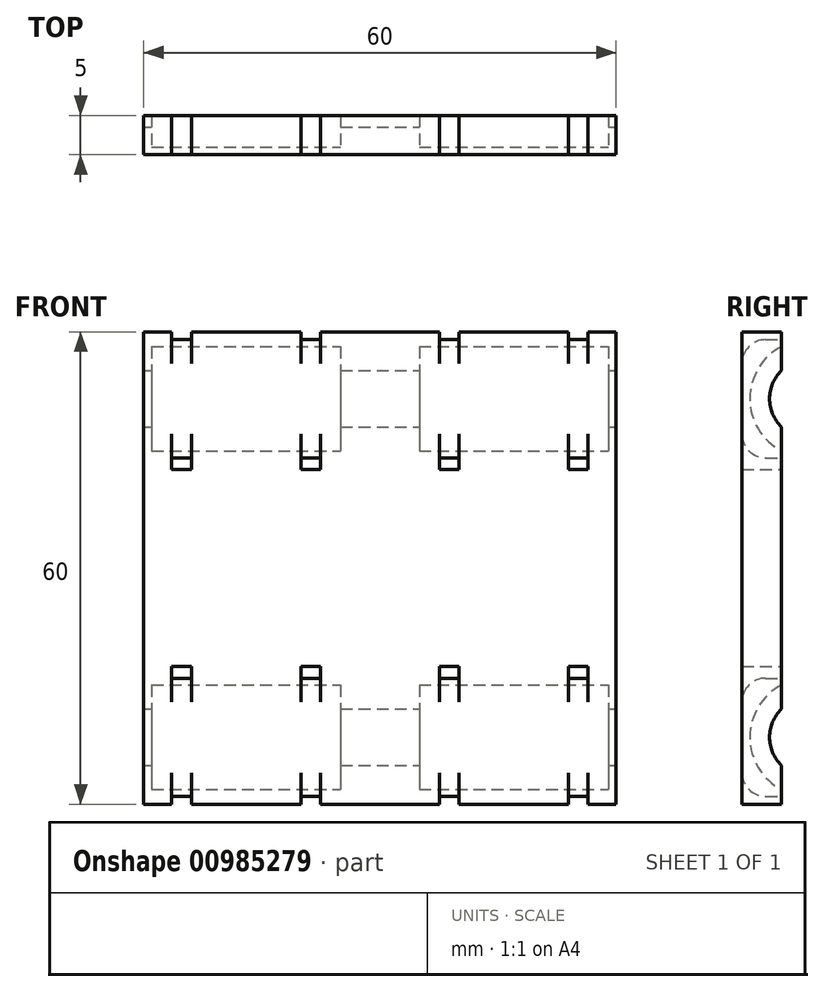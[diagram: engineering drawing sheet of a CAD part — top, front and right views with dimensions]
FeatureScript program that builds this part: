
annotation { "Feature Type Name" : "Feature", "Feature Type Description" : "" }
export const myFeature = defineFeature(function(context is Context, id is Id, definition is map)
    precondition{}
    {
        {
            var Q0;
            Q0=qCreatedBy(makeId("Front.planeOp"),FACE);
            var sketch = newSketch(context, id + "F0", { "sketchPlane" : qUnion([Q0])});
            skLineSegment(sketch, "E0.bottom", {"start": v(30, 30) * mm, "end": v(-30, 30) * mm});
            skLineSegment(sketch, "E0.top", {"start": v(30, -30) * mm, "end": v(-30, -30) * mm});
            skLineSegment(sketch, "E0.left", {"start": v(30, 30) * mm, "end": v(30, -30) * mm});
            skLineSegment(sketch, "E0.right", {"start": v(-30, 30) * mm, "end": v(-30, -30) * mm});
            skPoint(sketch, "E0.middle", {"position": v(0, 0) * mm});
            skSolve(sketch);
        }
        {
            var Q0;
            Q0 = qSketchRegion(id + "F0", true);
            extrude(context, id + "F1", {"entities" : qUnion([Q0]), "depth" : 5 * mm, "offsetDistance" : 25 * mm});
        }
        {
            var Q0;
            Q0=makeQuery(id+"F1.opExtrude","SWEPT_FACE",FACE,{"disambiguationData":[OSD([sQuery(id+"F0.wireOp",EDGE,"E0.left")])]});
            var sketch = newSketch(context, id + "F2", { "sketchPlane" : qUnion([Q0])});
            skCircle(sketch, "E1", {"center": v(3.5, 21.5) * mm, "radius": 7.5 * mm});
            skCircle(sketch, "E2.MirrorC", {"center": v(3.5, -21.5) * mm, "radius": 7.5 * mm});
            skSolve(sketch);
        }
        {
            var Q0;
            Q0 = qSketchRegion(id + "F2", true);
            extrude(context, id + "F3", {"entities" : qUnion([Q0]), "operationType" : NewBodyOperationType.REMOVE, "endBound" : BoundingType.THROUGH_ALL, "oppositeDirection" : true, "depth" : 25 * mm, "offsetDistance" : 25 * mm});
        }
        {
            var Q0;
            {var subQ0=sQuery(id+"F0.wireOp",EDGE,"E0.left");var subQ1=sQuery(id+"F0.wireOp",EDGE,"E0.right");Q0=makeQuery(id+"F3.boolean.opBoolean","SPLIT",FACE,{"disambiguationData":[TD([makeQuery(id+"F1.opExtrude","SWEPT_FACE",FACE,{"disambiguationData":[OSD([subQ0])]}),makeQuery(id+"F1.opExtrude","SWEPT_FACE",FACE,{"disambiguationData":[OSD([subQ1])]}),makeQuery(id+"F3.opExtrude","SWEPT_FACE",FACE,{"disambiguationData":[OSD([sQuery(id+"F2.wireOp",EDGE,"E1")])]}),makeQuery(id+"F3.opExtrude","SWEPT_FACE",FACE,{"disambiguationData":[OSD([sQuery(id+"F2.wireOp",EDGE,"E2.MirrorC")])]})])],"derivedFrom":makeQuery(id+"F1.opExtrude","CAP_FACE",FACE,{"disambiguationData":[OSD([sQuery(id+"F0.wireOp",EDGE,"E0.bottom"),sQuery(id+"F0.wireOp",EDGE,"E0.top"),subQ0,subQ1])],"isStart":true})});}
            var sketch = newSketch(context, id + "F4", { "sketchPlane" : qUnion([Q0])});
            skLineSegment(sketch, "E3.bottom", {"start": v(-30, 30) * mm, "end": v(-29, 30) * mm});
            skLineSegment(sketch, "E3.top", {"start": v(-30, -30) * mm, "end": v(-29, -30) * mm});
            skLineSegment(sketch, "E3.left", {"start": v(-30, 30) * mm, "end": v(-30, -30) * mm});
            skLineSegment(sketch, "E3.right", {"start": v(-29, 30) * mm, "end": v(-29, -30) * mm});
            skLineSegment(sketch, "E4.bottom", {"start": v(-5, 30) * mm, "end": v(5, 30) * mm});
            skLineSegment(sketch, "E4.top", {"start": v(-5, -30) * mm, "end": v(5, -30) * mm});
            skLineSegment(sketch, "E4.left", {"start": v(-5, 30) * mm, "end": v(-5, -30) * mm});
            skLineSegment(sketch, "E4.right", {"start": v(5, 30) * mm, "end": v(5, -30) * mm});
            skLineSegment(sketch, "E5.bottom", {"start": v(29, 30) * mm, "end": v(30, 30) * mm});
            skLineSegment(sketch, "E5.top", {"start": v(29, -30) * mm, "end": v(30, -30) * mm});
            skLineSegment(sketch, "E5.left", {"start": v(29, 30) * mm, "end": v(29, -30) * mm});
            skLineSegment(sketch, "E5.right", {"start": v(30, 30) * mm, "end": v(30, -30) * mm});
            skSolve(sketch);
        }
        {
            var Q0;
            Q0 = qSketchRegion(id + "F4", true);
            extrude(context, id + "F5", {"entities" : qUnion([Q0]), "operationType" : NewBodyOperationType.ADD, "oppositeDirection" : true, "depth" : 5 * mm, "offsetDistance" : 25 * mm});
        }
        {
            var Q0;
            Q0=makeQuery(id+"F5.boolean.opBoolean","MERGE",FACE,{"derivedFrom":[makeQuery(id+"F1.opExtrude","SWEPT_FACE",FACE,{"disambiguationData":[OSD([sQuery(id+"F0.wireOp",EDGE,"E0.left")])]}),makeQuery(id+"F5.opExtrude","SWEPT_FACE",FACE,{"disambiguationData":[OSD([sQuery(id+"F4.wireOp",EDGE,"E3.left")])]})]});
            var sketch = newSketch(context, id + "F6", { "sketchPlane" : qUnion([Q0])});
            skCircle(sketch, "E6", {"center": v(3.5, 21.5) * mm, "radius": 5 * mm});
            skCircle(sketch, "E7.MirrorC", {"center": v(3.5, -21.5) * mm, "radius": 5 * mm});
            skSolve(sketch);
        }
        {
            var Q0;
            Q0 = qSketchRegion(id + "F6", true);
            extrude(context, id + "F7", {"entities" : qUnion([Q0]), "operationType" : NewBodyOperationType.REMOVE, "endBound" : BoundingType.THROUGH_ALL, "oppositeDirection" : true, "depth" : 25 * mm, "offsetDistance" : 25 * mm});
        }
        {
            var Q0;
            {var subQ0=sQuery(id+"F4.wireOp",EDGE,"E3.left");var subQ1=sQuery(id+"F4.wireOp",EDGE,"E5.left");var subQ2=sQuery(id+"F4.wireOp",EDGE,"E3.right");var subQ3=sQuery(id+"F0.wireOp",EDGE,"E0.left");var subQ4=makeQuery(id+"F1.opExtrude","SWEPT_FACE",FACE,{"disambiguationData":[OSD([subQ3])]});var subQ5=sQuery(id+"F4.wireOp",EDGE,"E5.right");var subQ6=sQuery(id+"F0.wireOp",EDGE,"E0.right");var subQ7=makeQuery(id+"F1.opExtrude","SWEPT_FACE",FACE,{"disambiguationData":[OSD([subQ6])]});var subQ8=sQuery(id+"F4.wireOp",EDGE,"E4.left");var subQ9=makeQuery(id+"F3.opExtrude","SWEPT_FACE",FACE,{"disambiguationData":[OSD([sQuery(id+"F2.wireOp",EDGE,"E1")])]});var subQ10=sQuery(id+"F4.wireOp",EDGE,"E4.right");var subQ11=makeQuery(id+"F3.opExtrude","SWEPT_FACE",FACE,{"disambiguationData":[OSD([sQuery(id+"F2.wireOp",EDGE,"E2.MirrorC")])]});var subQ12=sQuery(id+"F0.wireOp",EDGE,"E0.top");var subQ13=sQuery(id+"F0.wireOp",EDGE,"E0.bottom");var subQ14=makeQuery(id+"F1.opExtrude","CAP_FACE",FACE,{"disambiguationData":[OSD([subQ13,subQ12,subQ3,subQ6])],"isStart":true});Q0=makeQuery(id+"F7.boolean.opBoolean","SPLIT",FACE,{"disambiguationData":[TD([subQ4,subQ7,makeQuery(id+"F3.boolean.opBoolean","COPY",FACE,{"derivedFrom":subQ9}),makeQuery(id+"F3.boolean.opBoolean","COPY",FACE,{"derivedFrom":subQ11}),makeQuery(id+"F5.opExtrude","SWEPT_FACE",FACE,{"disambiguationData":[OSD([subQ0])]}),makeQuery(id+"F5.opExtrude","SWEPT_FACE",FACE,{"disambiguationData":[OSD([subQ2])]}),makeQuery(id+"F5.opExtrude","SWEPT_FACE",FACE,{"disambiguationData":[OSD([subQ8])]}),makeQuery(id+"F5.opExtrude","SWEPT_FACE",FACE,{"disambiguationData":[OSD([subQ10])]}),makeQuery(id+"F5.opExtrude","SWEPT_FACE",FACE,{"disambiguationData":[OSD([subQ1])]}),makeQuery(id+"F5.opExtrude","SWEPT_FACE",FACE,{"disambiguationData":[OSD([subQ5])]}),makeQuery(id+"F7.opExtrude","SWEPT_FACE",FACE,{"disambiguationData":[OSD([sQuery(id+"F6.wireOp",EDGE,"E6")])]}),makeQuery(id+"F7.opExtrude","SWEPT_FACE",FACE,{"disambiguationData":[OSD([sQuery(id+"F6.wireOp",EDGE,"E7.MirrorC")])]})])],"derivedFrom":makeQuery(id+"F5.boolean.opBoolean","MERGE",FACE,{"derivedFrom":[makeQuery(id+"F3.boolean.opBoolean","SPLIT",FACE,{"disambiguationData":[TD([makeQuery(id+"F1.opExtrude","SWEPT_FACE",FACE,{"disambiguationData":[OSD([subQ13])]}),subQ4,subQ7,subQ9])],"derivedFrom":subQ14}),makeQuery(id+"F3.boolean.opBoolean","SPLIT",FACE,{"disambiguationData":[TD([makeQuery(id+"F1.opExtrude","SWEPT_FACE",FACE,{"disambiguationData":[OSD([subQ12])]}),subQ4,subQ7,subQ11])],"derivedFrom":subQ14}),makeQuery(id+"F3.boolean.opBoolean","SPLIT",FACE,{"disambiguationData":[TD([subQ4,subQ7,subQ9,subQ11])],"derivedFrom":subQ14}),makeQuery(id+"F5.opExtrude","CAP_FACE",FACE,{"disambiguationData":[OSD([sQuery(id+"F4.wireOp",EDGE,"E3.bottom"),sQuery(id+"F4.wireOp",EDGE,"E3.top"),subQ0,subQ2])],"isStart":true}),makeQuery(id+"F5.opExtrude","CAP_FACE",FACE,{"disambiguationData":[OSD([sQuery(id+"F4.wireOp",EDGE,"E4.bottom"),sQuery(id+"F4.wireOp",EDGE,"E4.top"),subQ8,subQ10])],"isStart":true}),makeQuery(id+"F5.opExtrude","CAP_FACE",FACE,{"disambiguationData":[OSD([sQuery(id+"F4.wireOp",EDGE,"E5.bottom"),sQuery(id+"F4.wireOp",EDGE,"E5.top"),subQ1,subQ5])],"isStart":true})]})});}
            var sketch = newSketch(context, id + "F8", { "sketchPlane" : qUnion([Q0])});
            skLineSegment(sketch, "E8.bottom", {"start": v(-26.45, 14) * mm, "end": v(-23.95, 14) * mm});
            skLineSegment(sketch, "E8.top", {"start": v(-26.45, 12.5) * mm, "end": v(-23.95, 12.5) * mm});
            skLineSegment(sketch, "E8.left", {"start": v(-26.45, 14) * mm, "end": v(-26.45, 12.5) * mm});
            skLineSegment(sketch, "E8.right", {"start": v(-23.95, 14) * mm, "end": v(-23.95, 12.5) * mm});
            skLineSegment(sketch, "E9.bottom", {"start": v(-10.05, 14) * mm, "end": v(-7.55, 14) * mm});
            skLineSegment(sketch, "E9.top", {"start": v(-10.05, 12.5) * mm, "end": v(-7.55, 12.5) * mm});
            skLineSegment(sketch, "E9.left", {"start": v(-10.05, 14) * mm, "end": v(-10.05, 12.5) * mm});
            skLineSegment(sketch, "E9.right", {"start": v(-7.55, 14) * mm, "end": v(-7.55, 12.5) * mm});
            skLineSegment(sketch, "E10.bottom", {"start": v(-10.05, 30.5) * mm, "end": v(-7.55, 30.5) * mm});
            skLineSegment(sketch, "E10.top", {"start": v(-10.05, 29) * mm, "end": v(-7.55, 29) * mm});
            skLineSegment(sketch, "E10.left", {"start": v(-10.05, 30.5) * mm, "end": v(-10.05, 29) * mm});
            skLineSegment(sketch, "E10.right", {"start": v(-7.55, 30.5) * mm, "end": v(-7.55, 29) * mm});
            skLineSegment(sketch, "E11.bottom", {"start": v(-26.45, 30.5) * mm, "end": v(-23.95, 30.5) * mm});
            skLineSegment(sketch, "E11.top", {"start": v(-26.45, 29) * mm, "end": v(-23.95, 29) * mm});
            skLineSegment(sketch, "E11.left", {"start": v(-26.45, 30.5) * mm, "end": v(-26.45, 29) * mm});
            skLineSegment(sketch, "E11.right", {"start": v(-23.95, 30.5) * mm, "end": v(-23.95, 29) * mm});
            skLineSegment(sketch, "E12", {"start": v(-34.92, 21.5) * mm, "end": v(-1.44, 21.5) * mm, "construction": true});
            skLineSegment(sketch, "E13.MirrorCS", {"start": v(26.45, 30.5) * mm, "end": v(26.45, 29) * mm});
            skLineSegment(sketch, "E14.MirrorCS", {"start": v(10.05, 14) * mm, "end": v(10.05, 12.5) * mm});
            skLineSegment(sketch, "E15.MirrorCS", {"start": v(7.55, 14) * mm, "end": v(7.55, 12.5) * mm});
            skLineSegment(sketch, "E16.MirrorCS", {"start": v(10.05, 30.5) * mm, "end": v(10.05, 29) * mm});
            skLineSegment(sketch, "E17.MirrorCS", {"start": v(23.95, 30.5) * mm, "end": v(23.95, 29) * mm});
            skLineSegment(sketch, "E18.MirrorCS", {"start": v(7.55, 30.5) * mm, "end": v(7.55, 29) * mm});
            skLineSegment(sketch, "E19.MirrorCS", {"start": v(23.95, 14) * mm, "end": v(23.95, 12.5) * mm});
            skLineSegment(sketch, "E20.MirrorCS", {"start": v(26.45, 14) * mm, "end": v(26.45, 12.5) * mm});
            skLineSegment(sketch, "E21.MirrorCS", {"start": v(10.05, 12.5) * mm, "end": v(7.55, 12.5) * mm});
            skLineSegment(sketch, "E22.MirrorCS", {"start": v(10.05, 14) * mm, "end": v(7.55, 14) * mm});
            skLineSegment(sketch, "E23.MirrorCS", {"start": v(26.45, 30.5) * mm, "end": v(23.95, 30.5) * mm});
            skLineSegment(sketch, "E24.MirrorCS", {"start": v(10.05, 29) * mm, "end": v(7.55, 29) * mm});
            skLineSegment(sketch, "E25.MirrorCS", {"start": v(26.45, 12.5) * mm, "end": v(23.95, 12.5) * mm});
            skLineSegment(sketch, "E26.MirrorCS", {"start": v(10.05, 30.5) * mm, "end": v(7.55, 30.5) * mm});
            skLineSegment(sketch, "E27.MirrorCS", {"start": v(26.45, 14) * mm, "end": v(23.95, 14) * mm});
            skLineSegment(sketch, "E28.MirrorCS", {"start": v(26.45, 29) * mm, "end": v(23.95, 29) * mm});
            skLineSegment(sketch, "E29.MirrorCS", {"start": v(-7.55, -14) * mm, "end": v(-7.55, -12.5) * mm});
            skLineSegment(sketch, "E30.MirrorCS", {"start": v(7.55, -30.5) * mm, "end": v(7.55, -29) * mm});
            skLineSegment(sketch, "E31.MirrorCS", {"start": v(23.95, -14) * mm, "end": v(23.95, -12.5) * mm});
            skLineSegment(sketch, "E32.MirrorCS", {"start": v(23.95, -30.5) * mm, "end": v(23.95, -29) * mm});
            skLineSegment(sketch, "E33.MirrorCS", {"start": v(10.05, -14) * mm, "end": v(10.05, -12.5) * mm});
            skLineSegment(sketch, "E34.MirrorCS", {"start": v(-26.45, -14) * mm, "end": v(-26.45, -12.5) * mm});
            skLineSegment(sketch, "E35.MirrorCS", {"start": v(-23.95, -30.5) * mm, "end": v(-23.95, -29) * mm});
            skLineSegment(sketch, "E36.MirrorCS", {"start": v(-7.55, -30.5) * mm, "end": v(-7.55, -29) * mm});
            skLineSegment(sketch, "E37.MirrorCS", {"start": v(-10.05, -30.5) * mm, "end": v(-10.05, -29) * mm});
            skLineSegment(sketch, "E38.MirrorCS", {"start": v(7.55, -14) * mm, "end": v(7.55, -12.5) * mm});
            skLineSegment(sketch, "E39.MirrorCS", {"start": v(-10.05, -14) * mm, "end": v(-10.05, -12.5) * mm});
            skLineSegment(sketch, "E40.MirrorCS", {"start": v(26.45, -30.5) * mm, "end": v(26.45, -29) * mm});
            skLineSegment(sketch, "E41.MirrorCS", {"start": v(-23.95, -14) * mm, "end": v(-23.95, -12.5) * mm});
            skLineSegment(sketch, "E42.MirrorCS", {"start": v(10.05, -30.5) * mm, "end": v(10.05, -29) * mm});
            skLineSegment(sketch, "E43.MirrorCS", {"start": v(26.45, -14) * mm, "end": v(26.45, -12.5) * mm});
            skLineSegment(sketch, "E44.MirrorCS", {"start": v(-26.45, -30.5) * mm, "end": v(-26.45, -29) * mm});
            skLineSegment(sketch, "E45.MirrorCS", {"start": v(-26.45, -12.5) * mm, "end": v(-23.95, -12.5) * mm});
            skLineSegment(sketch, "E46.MirrorCS", {"start": v(-10.05, -30.5) * mm, "end": v(-7.55, -30.5) * mm});
            skLineSegment(sketch, "E47.MirrorCS", {"start": v(-26.45, -14) * mm, "end": v(-23.95, -14) * mm});
            skLineSegment(sketch, "E48.MirrorCS", {"start": v(-10.05, -29) * mm, "end": v(-7.55, -29) * mm});
            skLineSegment(sketch, "E49.MirrorCS", {"start": v(-10.05, -14) * mm, "end": v(-7.55, -14) * mm});
            skLineSegment(sketch, "E50.MirrorCS", {"start": v(-26.45, -30.5) * mm, "end": v(-23.95, -30.5) * mm});
            skLineSegment(sketch, "E51.MirrorCS", {"start": v(10.05, -30.5) * mm, "end": v(7.55, -30.5) * mm});
            skLineSegment(sketch, "E52.MirrorCS", {"start": v(26.45, -29) * mm, "end": v(23.95, -29) * mm});
            skLineSegment(sketch, "E53.MirrorCS", {"start": v(10.05, -14) * mm, "end": v(7.55, -14) * mm});
            skLineSegment(sketch, "E54.MirrorCS", {"start": v(10.05, -12.5) * mm, "end": v(7.55, -12.5) * mm});
            skLineSegment(sketch, "E55.MirrorCS", {"start": v(-10.05, -12.5) * mm, "end": v(-7.55, -12.5) * mm});
            skLineSegment(sketch, "E56.MirrorCS", {"start": v(26.45, -14) * mm, "end": v(23.95, -14) * mm});
            skLineSegment(sketch, "E57.MirrorCS", {"start": v(26.45, -12.5) * mm, "end": v(23.95, -12.5) * mm});
            skLineSegment(sketch, "E58.MirrorCS", {"start": v(-26.45, -29) * mm, "end": v(-23.95, -29) * mm});
            skLineSegment(sketch, "E59.MirrorCS", {"start": v(26.45, -30.5) * mm, "end": v(23.95, -30.5) * mm});
            skLineSegment(sketch, "E60.MirrorCS", {"start": v(10.05, -29) * mm, "end": v(7.55, -29) * mm});
            skSolve(sketch);
        }
        {
            var Q0;
            Q0 = qSketchRegion(id + "F8", true);
            extrude(context, id + "F9", {"entities" : qUnion([Q0]), "operationType" : NewBodyOperationType.REMOVE, "endBound" : BoundingType.THROUGH_ALL, "oppositeDirection" : true, "depth" : 25 * mm, "offsetDistance" : 25 * mm});
        }
        {
            var Q0;
            Q0=makeQuery(id+"F9.boolean.opBoolean","INTERSECT",EDGE,{"derivedFrom":[makeQuery(id+"F1.opExtrude","CAP_FACE",FACE,{"disambiguationData":[OSD([sQuery(id+"F0.wireOp",EDGE,"E0.bottom"),sQuery(id+"F0.wireOp",EDGE,"E0.top"),sQuery(id+"F0.wireOp",EDGE,"E0.left"),sQuery(id+"F0.wireOp",EDGE,"E0.right")])],"isStart":false}),makeQuery(id+"F9.opExtrude","SWEPT_FACE",FACE,{"disambiguationData":[OSD([sQuery(id+"F8.wireOp",EDGE,"E58.MirrorCS")])]})]});
            var Q1;
            Q1=makeQuery(id+"F9.boolean.opBoolean","INTERSECT",EDGE,{"derivedFrom":[makeQuery(id+"F1.opExtrude","CAP_FACE",FACE,{"disambiguationData":[OSD([sQuery(id+"F0.wireOp",EDGE,"E0.bottom"),sQuery(id+"F0.wireOp",EDGE,"E0.top"),sQuery(id+"F0.wireOp",EDGE,"E0.left"),sQuery(id+"F0.wireOp",EDGE,"E0.right")])],"isStart":false}),makeQuery(id+"F9.opExtrude","SWEPT_FACE",FACE,{"disambiguationData":[OSD([sQuery(id+"F8.wireOp",EDGE,"E47.MirrorCS")])]})]});
            var Q2;
            Q2=makeQuery(id+"F9.boolean.opBoolean","INTERSECT",EDGE,{"derivedFrom":[makeQuery(id+"F1.opExtrude","CAP_FACE",FACE,{"disambiguationData":[OSD([sQuery(id+"F0.wireOp",EDGE,"E0.bottom"),sQuery(id+"F0.wireOp",EDGE,"E0.top"),sQuery(id+"F0.wireOp",EDGE,"E0.left"),sQuery(id+"F0.wireOp",EDGE,"E0.right")])],"isStart":false}),makeQuery(id+"F9.opExtrude","SWEPT_FACE",FACE,{"disambiguationData":[OSD([sQuery(id+"F8.wireOp",EDGE,"E49.MirrorCS")])]})]});
            var Q3;
            Q3=makeQuery(id+"F9.boolean.opBoolean","INTERSECT",EDGE,{"derivedFrom":[makeQuery(id+"F1.opExtrude","CAP_FACE",FACE,{"disambiguationData":[OSD([sQuery(id+"F0.wireOp",EDGE,"E0.bottom"),sQuery(id+"F0.wireOp",EDGE,"E0.top"),sQuery(id+"F0.wireOp",EDGE,"E0.left"),sQuery(id+"F0.wireOp",EDGE,"E0.right")])],"isStart":false}),makeQuery(id+"F9.opExtrude","SWEPT_FACE",FACE,{"disambiguationData":[OSD([sQuery(id+"F8.wireOp",EDGE,"E48.MirrorCS")])]})]});
            var Q4;
            Q4=makeQuery(id+"F9.boolean.opBoolean","INTERSECT",EDGE,{"derivedFrom":[makeQuery(id+"F1.opExtrude","CAP_FACE",FACE,{"disambiguationData":[OSD([sQuery(id+"F0.wireOp",EDGE,"E0.bottom"),sQuery(id+"F0.wireOp",EDGE,"E0.top"),sQuery(id+"F0.wireOp",EDGE,"E0.left"),sQuery(id+"F0.wireOp",EDGE,"E0.right")])],"isStart":false}),makeQuery(id+"F9.opExtrude","SWEPT_FACE",FACE,{"disambiguationData":[OSD([sQuery(id+"F8.wireOp",EDGE,"E60.MirrorCS")])]})]});
            var Q5;
            Q5=makeQuery(id+"F9.boolean.opBoolean","INTERSECT",EDGE,{"derivedFrom":[makeQuery(id+"F1.opExtrude","CAP_FACE",FACE,{"disambiguationData":[OSD([sQuery(id+"F0.wireOp",EDGE,"E0.bottom"),sQuery(id+"F0.wireOp",EDGE,"E0.top"),sQuery(id+"F0.wireOp",EDGE,"E0.left"),sQuery(id+"F0.wireOp",EDGE,"E0.right")])],"isStart":false}),makeQuery(id+"F9.opExtrude","SWEPT_FACE",FACE,{"disambiguationData":[OSD([sQuery(id+"F8.wireOp",EDGE,"E53.MirrorCS")])]})]});
            var Q6;
            Q6=makeQuery(id+"F9.boolean.opBoolean","INTERSECT",EDGE,{"derivedFrom":[makeQuery(id+"F1.opExtrude","CAP_FACE",FACE,{"disambiguationData":[OSD([sQuery(id+"F0.wireOp",EDGE,"E0.bottom"),sQuery(id+"F0.wireOp",EDGE,"E0.top"),sQuery(id+"F0.wireOp",EDGE,"E0.left"),sQuery(id+"F0.wireOp",EDGE,"E0.right")])],"isStart":false}),makeQuery(id+"F9.opExtrude","SWEPT_FACE",FACE,{"disambiguationData":[OSD([sQuery(id+"F8.wireOp",EDGE,"E56.MirrorCS")])]})]});
            var Q7;
            Q7=makeQuery(id+"F9.boolean.opBoolean","INTERSECT",EDGE,{"derivedFrom":[makeQuery(id+"F1.opExtrude","CAP_FACE",FACE,{"disambiguationData":[OSD([sQuery(id+"F0.wireOp",EDGE,"E0.bottom"),sQuery(id+"F0.wireOp",EDGE,"E0.top"),sQuery(id+"F0.wireOp",EDGE,"E0.left"),sQuery(id+"F0.wireOp",EDGE,"E0.right")])],"isStart":false}),makeQuery(id+"F9.opExtrude","SWEPT_FACE",FACE,{"disambiguationData":[OSD([sQuery(id+"F8.wireOp",EDGE,"E52.MirrorCS")])]})]});
            var Q8;
            Q8=makeQuery(id+"F9.boolean.opBoolean","INTERSECT",EDGE,{"derivedFrom":[makeQuery(id+"F1.opExtrude","CAP_FACE",FACE,{"disambiguationData":[OSD([sQuery(id+"F0.wireOp",EDGE,"E0.bottom"),sQuery(id+"F0.wireOp",EDGE,"E0.top"),sQuery(id+"F0.wireOp",EDGE,"E0.left"),sQuery(id+"F0.wireOp",EDGE,"E0.right")])],"isStart":false}),makeQuery(id+"F9.opExtrude","SWEPT_FACE",FACE,{"disambiguationData":[OSD([sQuery(id+"F8.wireOp",EDGE,"E27.MirrorCS")])]})]});
            var Q9;
            Q9=makeQuery(id+"F9.boolean.opBoolean","INTERSECT",EDGE,{"derivedFrom":[makeQuery(id+"F1.opExtrude","CAP_FACE",FACE,{"disambiguationData":[OSD([sQuery(id+"F0.wireOp",EDGE,"E0.bottom"),sQuery(id+"F0.wireOp",EDGE,"E0.top"),sQuery(id+"F0.wireOp",EDGE,"E0.left"),sQuery(id+"F0.wireOp",EDGE,"E0.right")])],"isStart":false}),makeQuery(id+"F9.opExtrude","SWEPT_FACE",FACE,{"disambiguationData":[OSD([sQuery(id+"F8.wireOp",EDGE,"E22.MirrorCS")])]})]});
            var Q10;
            Q10=makeQuery(id+"F9.boolean.opBoolean","INTERSECT",EDGE,{"derivedFrom":[makeQuery(id+"F1.opExtrude","CAP_FACE",FACE,{"disambiguationData":[OSD([sQuery(id+"F0.wireOp",EDGE,"E0.bottom"),sQuery(id+"F0.wireOp",EDGE,"E0.top"),sQuery(id+"F0.wireOp",EDGE,"E0.left"),sQuery(id+"F0.wireOp",EDGE,"E0.right")])],"isStart":false}),makeQuery(id+"F9.opExtrude","SWEPT_FACE",FACE,{"disambiguationData":[OSD([sQuery(id+"F8.wireOp",EDGE,"E24.MirrorCS")])]})]});
            var Q11;
            Q11=makeQuery(id+"F9.boolean.opBoolean","INTERSECT",EDGE,{"derivedFrom":[makeQuery(id+"F1.opExtrude","CAP_FACE",FACE,{"disambiguationData":[OSD([sQuery(id+"F0.wireOp",EDGE,"E0.bottom"),sQuery(id+"F0.wireOp",EDGE,"E0.top"),sQuery(id+"F0.wireOp",EDGE,"E0.left"),sQuery(id+"F0.wireOp",EDGE,"E0.right")])],"isStart":false}),makeQuery(id+"F9.opExtrude","SWEPT_FACE",FACE,{"disambiguationData":[OSD([sQuery(id+"F8.wireOp",EDGE,"E28.MirrorCS")])]})]});
            var Q12;
            Q12=makeQuery(id+"F9.boolean.opBoolean","INTERSECT",EDGE,{"derivedFrom":[makeQuery(id+"F1.opExtrude","CAP_FACE",FACE,{"disambiguationData":[OSD([sQuery(id+"F0.wireOp",EDGE,"E0.bottom"),sQuery(id+"F0.wireOp",EDGE,"E0.top"),sQuery(id+"F0.wireOp",EDGE,"E0.left"),sQuery(id+"F0.wireOp",EDGE,"E0.right")])],"isStart":false}),makeQuery(id+"F9.opExtrude","SWEPT_FACE",FACE,{"disambiguationData":[OSD([sQuery(id+"F8.wireOp",EDGE,"E9.bottom")])]})]});
            var Q13;
            Q13=makeQuery(id+"F9.boolean.opBoolean","INTERSECT",EDGE,{"derivedFrom":[makeQuery(id+"F1.opExtrude","CAP_FACE",FACE,{"disambiguationData":[OSD([sQuery(id+"F0.wireOp",EDGE,"E0.bottom"),sQuery(id+"F0.wireOp",EDGE,"E0.top"),sQuery(id+"F0.wireOp",EDGE,"E0.left"),sQuery(id+"F0.wireOp",EDGE,"E0.right")])],"isStart":false}),makeQuery(id+"F9.opExtrude","SWEPT_FACE",FACE,{"disambiguationData":[OSD([sQuery(id+"F8.wireOp",EDGE,"E10.top")])]})]});
            var Q14;
            Q14=makeQuery(id+"F9.boolean.opBoolean","INTERSECT",EDGE,{"derivedFrom":[makeQuery(id+"F1.opExtrude","CAP_FACE",FACE,{"disambiguationData":[OSD([sQuery(id+"F0.wireOp",EDGE,"E0.bottom"),sQuery(id+"F0.wireOp",EDGE,"E0.top"),sQuery(id+"F0.wireOp",EDGE,"E0.left"),sQuery(id+"F0.wireOp",EDGE,"E0.right")])],"isStart":false}),makeQuery(id+"F9.opExtrude","SWEPT_FACE",FACE,{"disambiguationData":[OSD([sQuery(id+"F8.wireOp",EDGE,"E11.top")])]})]});
            var Q15;
            Q15=makeQuery(id+"F9.boolean.opBoolean","INTERSECT",EDGE,{"derivedFrom":[makeQuery(id+"F1.opExtrude","CAP_FACE",FACE,{"disambiguationData":[OSD([sQuery(id+"F0.wireOp",EDGE,"E0.bottom"),sQuery(id+"F0.wireOp",EDGE,"E0.top"),sQuery(id+"F0.wireOp",EDGE,"E0.left"),sQuery(id+"F0.wireOp",EDGE,"E0.right")])],"isStart":false}),makeQuery(id+"F9.opExtrude","SWEPT_FACE",FACE,{"disambiguationData":[OSD([sQuery(id+"F8.wireOp",EDGE,"E8.bottom")])]})]});
            fillet(context, id + "F10", {"entities" : qUnion([Q0, Q1, Q2, Q3, Q4, Q5, Q6, Q7, Q8, Q9, Q10, Q11, Q12, Q13, Q14, Q15]), "radius" : 3 * mm, "tangentPropagation" : true, "allowEdgeOverflow" : false});
        }
    });
